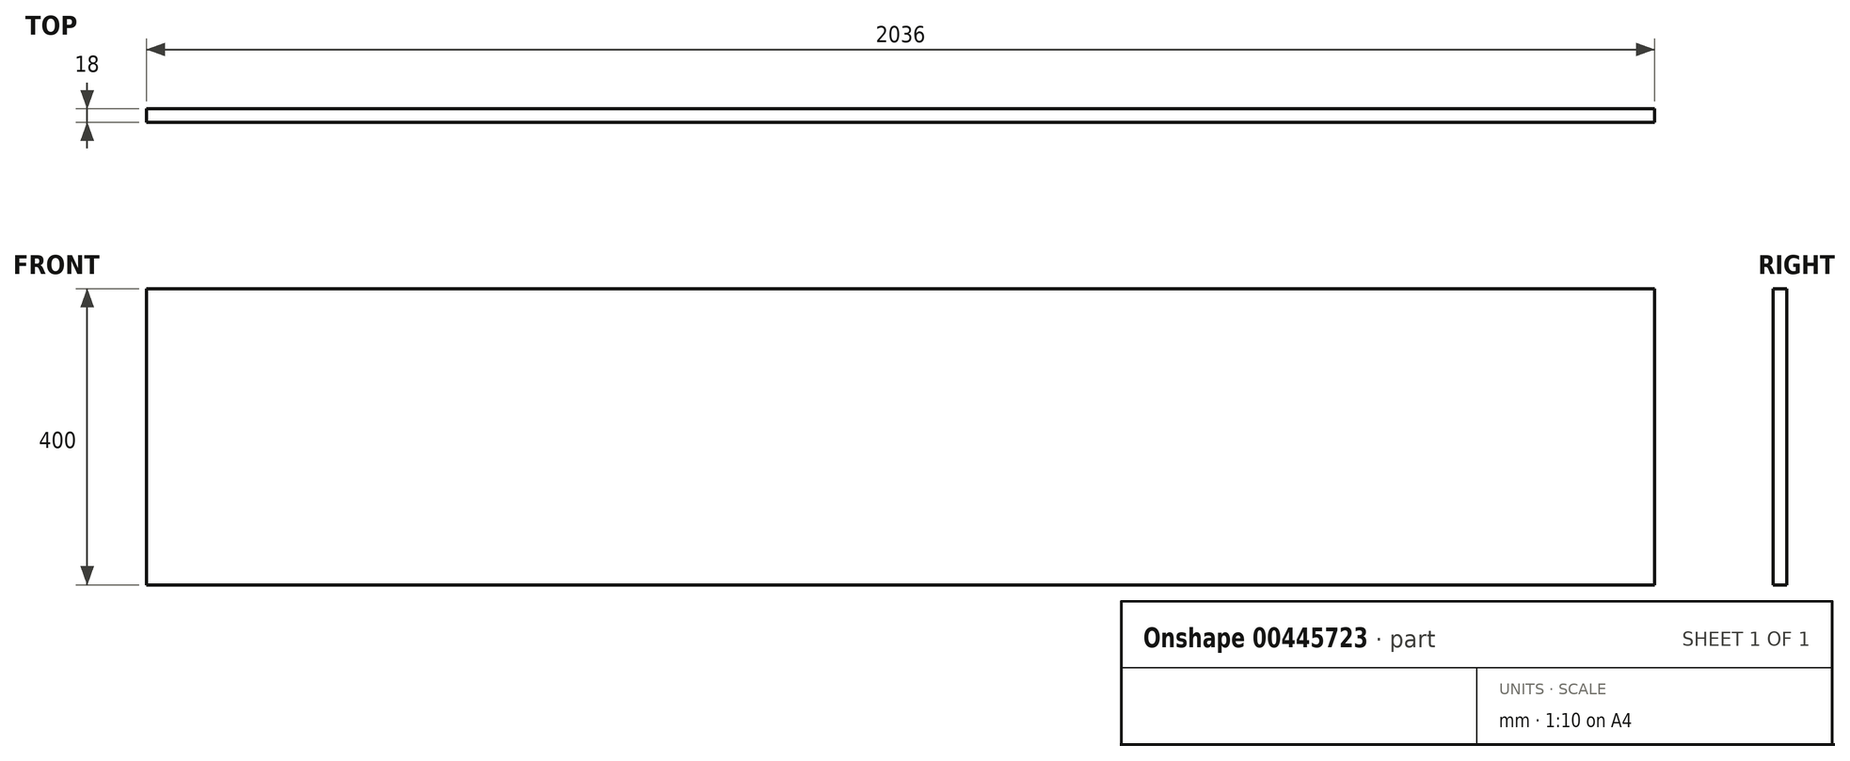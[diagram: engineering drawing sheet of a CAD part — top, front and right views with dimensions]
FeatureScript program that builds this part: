
annotation { "Feature Type Name" : "Feature", "Feature Type Description" : "" }
export const myFeature = defineFeature(function(context is Context, id is Id, definition is map)
    precondition{}
    {
        {
            var Q0;
            Q0=qCreatedBy(makeId("Front.planeOp"),FACE);
            var sketch = newSketch(context, id + "F0", { "sketchPlane" : qUnion([Q0])});
            skLineSegment(sketch, "E0.bottom", {"start": v(0, 0) * mm, "end": v(2036, 0) * mm});
            skLineSegment(sketch, "E0.top", {"start": v(0, -400) * mm, "end": v(2036, -400) * mm});
            skLineSegment(sketch, "E0.left", {"start": v(0, 0) * mm, "end": v(0, -400) * mm});
            skLineSegment(sketch, "E0.right", {"start": v(2036, 0) * mm, "end": v(2036, -400) * mm});
            skSolve(sketch);
        }
        {
            var Q0;
            Q0 = qSketchRegion(id + "F0", true);
            extrude(context, id + "F1", {"entities" : qUnion([Q0]), "depth" : 18 * mm});
        }
    });
